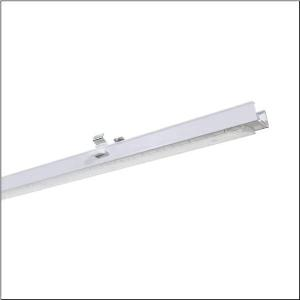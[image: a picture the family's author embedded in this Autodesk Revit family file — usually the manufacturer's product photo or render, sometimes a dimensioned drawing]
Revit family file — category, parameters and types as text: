
# Revit family: trunking_flex_31_51re11db4cb
name_source: partatom
category: Lighting Fixtures
units: mm (PartAtom-declared; Revit-internal decimal feet)

## family parameters
Cut with Voids When Loaded = No
Host = Face
Light Source = No
Part Type = Normal
Room Calculation Point = No
Round Connector Dimension = Use Diameter
Shared = No

## types (1)
- Trunking Flex 31 (1 x LED, 11500 lm, 66 W, 4000K)
    Apparent Load = 66 VA
    CIE Flux Codes = 83 93 98 100 100
    Color Rendering = 80
    Color Temperature = 4000K
    Default Elevation = 1800 mm
    Description = Trunking Flex 31, luminaire insert, of extruded aluminium section, coated, traffic white (RAL 9016), length: 1.472mm, width: 91mm, height: 53mm, LED rated luminous flux: 11.500lm, light colour: 840, control gear: DALI 2, with system connector: socket, mains connection: 220..240V, AC, 50/60Hz, rated input power: 66W, primary light control with lens, of plastic, primary optical cover: cover, of PMMA, light emission: direct distribution, protection rating (complete): IP20, insulation class (complete): insulation class I (protective earthing), certification: CE, UKCA, impact resistance: IK02, permissible ambient temperature for indoor applications: -20..+40°C, packaging unit: 1 piece
    Height = 58 mm
    Lamp = 1 x LED
    Lamp Light Flux = 11500 lm
    Lamp Power = 66 W
    Lamp count = 1
    Length = 1472 mm
    Luminous efficacy = 174 lm/W
    Manufacturer = Siteco
    ModVariant = No
    Model = 51RE11DB4CB
    Mounting Place = Ceiling
    Mounting Type = Pendant
    Number of Poles = 1
    OnlyDefault = Yes
    Power Factor = 1
    Product Name = Trunking Flex 31
    Product group = luminaire insert
    ProductGroupID = 901
    Protection Class = Protection class I
    Protection Degree = IP 20
    RLX_Detail_Level = 1
    RLX_Emergency_Light_Flux = 0 lm
    RLX_Emergency_Type = 0
    RLX_Emergency_Type_DB = No
    RlxData = <blob elided: 19481 chars, md5=141ae4e1>
    Socket = socket
    Standby Power = 0 W
    System Light Flux = 11500 lm
    System Power = 66 W
    Type Comments = Product without accessories
    Type Image = l_1266702.jpg
    URL = http://relux.com
    VarID = ---
    Voltage = 0 V
    Weight = 0.00 kg
    Width = 65 mm

## geometry (parser evidence)
native form markers: Blend x4, Sweep x12
no freeform markers — native parametric forms only
